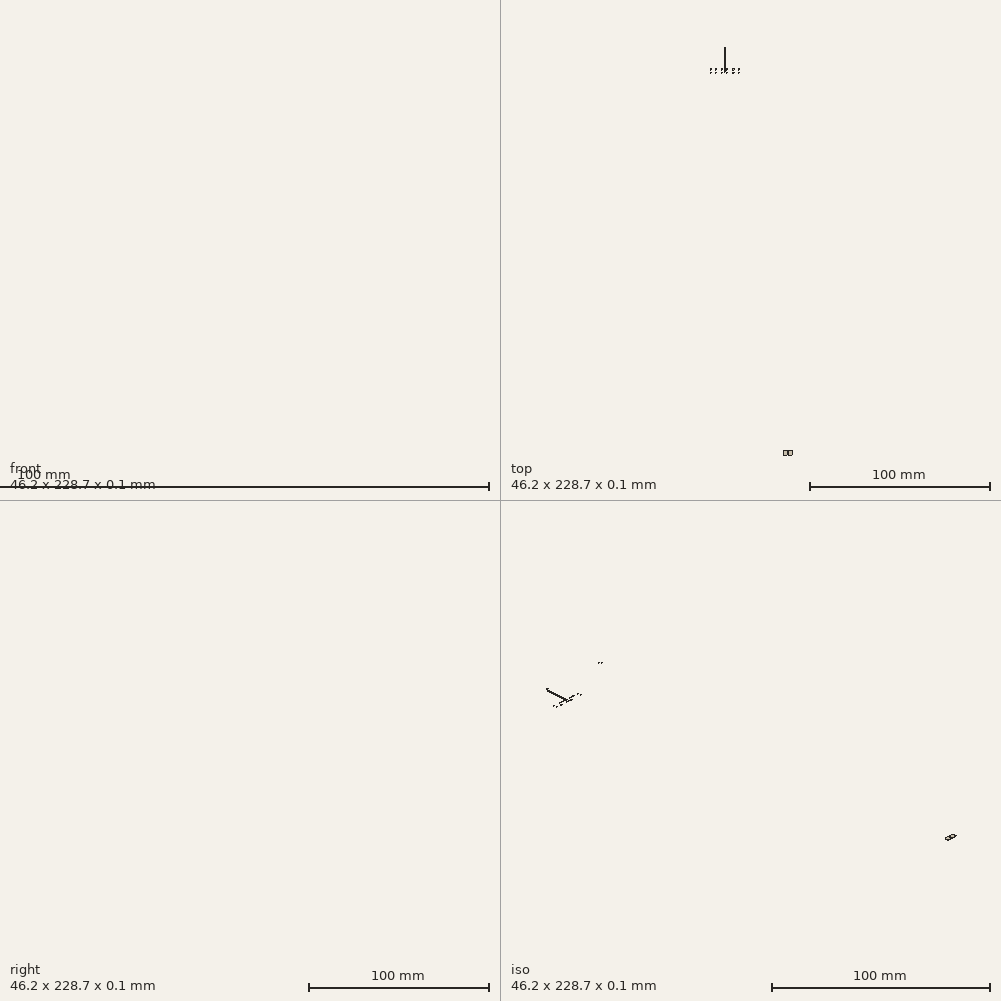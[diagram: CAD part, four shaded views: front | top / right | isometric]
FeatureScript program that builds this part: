
annotation { "Feature Type Name" : "Feature", "Feature Type Description" : "" }
export const myFeature = defineFeature(function(context is Context, id is Id, definition is map)
    precondition{}
    {
        {
            var Q0;
            Q0=qCreatedBy(makeId("Top.planeOp"),FACE);
            var sketch = newSketch(context, id + "F0", { "sketchPlane" : qUnion([Q0])});
            skLineSegment(sketch, "E0.bottom", {"start": v(0, 0) * mm, "end": v(3.5, 0) * mm, "construction": true});
            skLineSegment(sketch, "E0.top", {"start": v(0, 2.4) * mm, "end": v(3.5, 2.4) * mm, "construction": true});
            skLineSegment(sketch, "E0.left", {"start": v(0, 0) * mm, "end": v(0, 2.4) * mm, "construction": true});
            skLineSegment(sketch, "E0.right", {"start": v(3.5, 0) * mm, "end": v(3.5, 0.27) * mm, "construction": true});
            skLineSegment(sketch, "E1.bottom", {"start": v(0, 2.4) * mm, "end": v(0.6, 2.4) * mm});
            skLineSegment(sketch, "E1.top", {"start": v(0, 1.8) * mm, "end": v(0.6, 1.8) * mm});
            skLineSegment(sketch, "E1.left", {"start": v(0, 2.4) * mm, "end": v(0, 1.8) * mm});
            skLineSegment(sketch, "E1.right", {"start": v(0.6, 2.4) * mm, "end": v(0.6, 1.8) * mm});
            skLineSegment(sketch, "E2.bottom", {"start": v(0, 0) * mm, "end": v(0.6, 0) * mm});
            skLineSegment(sketch, "E2.top", {"start": v(0, 0.6) * mm, "end": v(0.6, 0.6) * mm});
            skLineSegment(sketch, "E2.left", {"start": v(0, 0) * mm, "end": v(0, 0.6) * mm});
            skLineSegment(sketch, "E2.right", {"start": v(0.6, 0) * mm, "end": v(0.6, 0.6) * mm});
            skLineSegment(sketch, "E3.bottom", {"start": v(3.5, 2.4) * mm, "end": v(2.9, 2.4) * mm});
            skLineSegment(sketch, "E3.top", {"start": v(3.5, 1.8) * mm, "end": v(2.9, 1.8) * mm});
            skLineSegment(sketch, "E3.left", {"start": v(3.5, 2.4) * mm, "end": v(3.5, 2.13) * mm});
            skLineSegment(sketch, "E3.right", {"start": v(2.9, 2.4) * mm, "end": v(2.9, 1.8) * mm});
            skLineSegment(sketch, "E4.bottom", {"start": v(3.5, 0) * mm, "end": v(2.9, 0) * mm});
            skLineSegment(sketch, "E4.top", {"start": v(3.5, 0.6) * mm, "end": v(2.9, 0.6) * mm});
            skLineSegment(sketch, "E4.left", {"start": v(3.5, 0) * mm, "end": v(3.5, 0.27) * mm});
            skLineSegment(sketch, "E4.right", {"start": v(2.9, 0) * mm, "end": v(2.9, 0.6) * mm});
            skLineSegment(sketch, "E5", {"start": v(0, 0) * mm, "end": v(16.26, 0) * mm, "construction": true});
            skLineSegment(sketch, "E6.bottom", {"start": v(12.76, 0) * mm, "end": v(16.26, 0) * mm, "construction": true});
            skLineSegment(sketch, "E6.top", {"start": v(12.76, 2.4) * mm, "end": v(16.26, 2.4) * mm, "construction": true});
            skLineSegment(sketch, "E6.right", {"start": v(16.26, 0) * mm, "end": v(16.26, 2.4) * mm, "construction": true});
            skLineSegment(sketch, "E7.bottom", {"start": v(12.76, 2.4) * mm, "end": v(13.36, 2.4) * mm});
            skLineSegment(sketch, "E7.top", {"start": v(12.76, 1.8) * mm, "end": v(13.36, 1.8) * mm});
            skLineSegment(sketch, "E7.left", {"start": v(12.76, 2.4) * mm, "end": v(12.76, 2.13) * mm});
            skLineSegment(sketch, "E7.right", {"start": v(13.36, 2.4) * mm, "end": v(13.36, 1.8) * mm});
            skLineSegment(sketch, "E8.bottom", {"start": v(12.76, 0) * mm, "end": v(13.36, 0) * mm});
            skLineSegment(sketch, "E8.top", {"start": v(12.76, 0.6) * mm, "end": v(13.36, 0.6) * mm});
            skLineSegment(sketch, "E8.left", {"start": v(12.76, 0) * mm, "end": v(12.76, 0.27) * mm});
            skLineSegment(sketch, "E8.right", {"start": v(13.36, 0) * mm, "end": v(13.36, 0.6) * mm});
            skLineSegment(sketch, "E9.bottom", {"start": v(16.26, 2.4) * mm, "end": v(15.66, 2.4) * mm});
            skLineSegment(sketch, "E9.top", {"start": v(16.26, 1.8) * mm, "end": v(15.66, 1.8) * mm});
            skLineSegment(sketch, "E9.left", {"start": v(16.26, 2.4) * mm, "end": v(16.26, 1.8) * mm});
            skLineSegment(sketch, "E9.right", {"start": v(15.66, 2.4) * mm, "end": v(15.66, 1.8) * mm});
            skLineSegment(sketch, "E10.bottom", {"start": v(16.26, 0) * mm, "end": v(15.66, 0) * mm});
            skLineSegment(sketch, "E10.top", {"start": v(16.26, 0.6) * mm, "end": v(15.66, 0.6) * mm});
            skLineSegment(sketch, "E10.left", {"start": v(16.26, 0) * mm, "end": v(16.26, 0.6) * mm});
            skLineSegment(sketch, "E10.right", {"start": v(15.66, 0) * mm, "end": v(15.66, 0.6) * mm});
            skLineSegment(sketch, "E11.bottom", {"start": v(6.38, 0) * mm, "end": v(9.88, 0) * mm, "construction": true});
            skLineSegment(sketch, "E11.top", {"start": v(6.38, 2.4) * mm, "end": v(9.88, 2.4) * mm, "construction": true});
            skLineSegment(sketch, "E11.left", {"start": v(6.38, 0) * mm, "end": v(6.38, 0.27) * mm, "construction": true});
            skLineSegment(sketch, "E12.bottom", {"start": v(6.38, 2.4) * mm, "end": v(6.98, 2.4) * mm});
            skLineSegment(sketch, "E12.top", {"start": v(6.38, 1.8) * mm, "end": v(6.98, 1.8) * mm});
            skLineSegment(sketch, "E12.left", {"start": v(6.38, 2.4) * mm, "end": v(6.38, 2.13) * mm});
            skLineSegment(sketch, "E12.right", {"start": v(6.98, 2.4) * mm, "end": v(6.98, 1.8) * mm});
            skLineSegment(sketch, "E13.bottom", {"start": v(6.38, 0) * mm, "end": v(6.98, 0) * mm});
            skLineSegment(sketch, "E13.top", {"start": v(6.38, 0.6) * mm, "end": v(6.98, 0.6) * mm});
            skLineSegment(sketch, "E13.left", {"start": v(6.38, 0) * mm, "end": v(6.38, 0.27) * mm});
            skLineSegment(sketch, "E13.right", {"start": v(6.98, 0) * mm, "end": v(6.98, 0.6) * mm});
            skLineSegment(sketch, "E14.bottom", {"start": v(9.88, 2.4) * mm, "end": v(9.28, 2.4) * mm});
            skLineSegment(sketch, "E14.top", {"start": v(9.88, 1.8) * mm, "end": v(9.28, 1.8) * mm});
            skLineSegment(sketch, "E14.left", {"start": v(9.88, 2.4) * mm, "end": v(9.88, 2.13) * mm});
            skLineSegment(sketch, "E14.right", {"start": v(9.28, 2.4) * mm, "end": v(9.28, 1.8) * mm});
            skLineSegment(sketch, "E15.bottom", {"start": v(9.88, 0) * mm, "end": v(9.28, 0) * mm});
            skLineSegment(sketch, "E15.top", {"start": v(9.88, 0.6) * mm, "end": v(9.28, 0.6) * mm});
            skLineSegment(sketch, "E15.left", {"start": v(9.88, 0) * mm, "end": v(9.88, 0.27) * mm});
            skLineSegment(sketch, "E15.right", {"start": v(9.28, 0) * mm, "end": v(9.28, 0.6) * mm});
            skPoint(sketch, "E16", {"position": v(8.13, 0) * mm});
            skLineSegment(sketch, "E17.bottom", {"start": v(3.5, 2.13) * mm, "end": v(6.38, 2.13) * mm});
            skLineSegment(sketch, "E17.top", {"start": v(3.5, 2.06) * mm, "end": v(6.38, 2.06) * mm});
            skLineSegment(sketch, "E18.bottom", {"start": v(3.5, 0.33) * mm, "end": v(6.38, 0.33) * mm});
            skLineSegment(sketch, "E18.top", {"start": v(3.5, 0.27) * mm, "end": v(6.38, 0.27) * mm});
            skLineSegment(sketch, "E19.trimOffspring", {"start": v(3.5, 2.13) * mm, "end": v(3.5, 2.4) * mm, "construction": true});
            skLineSegment(sketch, "E20.trimOffspring", {"start": v(3.5, 2.06) * mm, "end": v(3.5, 1.8) * mm});
            skLineSegment(sketch, "E21.trimOffspring", {"start": v(6.38, 2.13) * mm, "end": v(6.38, 2.4) * mm, "construction": true});
            skLineSegment(sketch, "E22.trimOffspring", {"start": v(6.38, 2.06) * mm, "end": v(6.38, 1.8) * mm});
            skLineSegment(sketch, "E23.trimOffspring", {"start": v(3.5, 0.33) * mm, "end": v(3.5, 2.06) * mm, "construction": true});
            skLineSegment(sketch, "E24.trimOffspring", {"start": v(3.5, 0.33) * mm, "end": v(3.5, 0.6) * mm});
            skLineSegment(sketch, "E25.trimOffspring", {"start": v(6.38, 0.33) * mm, "end": v(6.38, 2.06) * mm, "construction": true});
            skLineSegment(sketch, "E26.trimOffspring", {"start": v(6.38, 0.33) * mm, "end": v(6.38, 0.6) * mm});
            skLineSegment(sketch, "E27.bottom", {"start": v(9.88, 2.13) * mm, "end": v(12.76, 2.13) * mm});
            skLineSegment(sketch, "E27.top", {"start": v(9.88, 2.07) * mm, "end": v(12.76, 2.07) * mm});
            skLineSegment(sketch, "E28.bottom", {"start": v(9.88, 0.33) * mm, "end": v(12.76, 0.33) * mm});
            skLineSegment(sketch, "E28.top", {"start": v(9.88, 0.27) * mm, "end": v(12.76, 0.27) * mm});
            skLineSegment(sketch, "E29.trimOffspring", {"start": v(9.88, 0.33) * mm, "end": v(9.88, 0.6) * mm, "construction": true});
            skLineSegment(sketch, "E30.trimOffspring", {"start": v(9.88, 0.33) * mm, "end": v(9.88, 0.6) * mm});
            skLineSegment(sketch, "E31.trimOffspring", {"start": v(12.76, 0.33) * mm, "end": v(12.76, 2.07) * mm, "construction": true});
            skLineSegment(sketch, "E32.trimOffspring", {"start": v(12.76, 0.33) * mm, "end": v(12.76, 0.6) * mm});
            skLineSegment(sketch, "E33.trimOffspring", {"start": v(12.76, 2.13) * mm, "end": v(12.76, 2.4) * mm, "construction": true});
            skLineSegment(sketch, "E34.trimOffspring", {"start": v(12.76, 2.07) * mm, "end": v(12.76, 1.8) * mm});
            skLineSegment(sketch, "E35.trimOffspring", {"start": v(9.88, 2.13) * mm, "end": v(9.88, 2.4) * mm, "construction": true});
            skLineSegment(sketch, "E36.trimOffspring", {"start": v(9.88, 2.07) * mm, "end": v(9.88, 1.8) * mm});
            skLineSegment(sketch, "E37.bottom", {"start": v(6.98, 2.13) * mm, "end": v(7.92, 2.13) * mm});
            skLineSegment(sketch, "E37.top", {"start": v(6.98, 2.07) * mm, "end": v(7.92, 2.07) * mm});
            skLineSegment(sketch, "E37.left", {"start": v(6.98, 2.13) * mm, "end": v(6.98, 2.07) * mm});
            skLineSegment(sketch, "E37.right", {"start": v(7.92, 2.13) * mm, "end": v(7.92, 2.07) * mm});
            skLineSegment(sketch, "E38.bottom", {"start": v(9.28, 0.33) * mm, "end": v(8.33, 0.33) * mm});
            skLineSegment(sketch, "E38.top", {"start": v(9.28, 0.27) * mm, "end": v(8.33, 0.27) * mm});
            skLineSegment(sketch, "E38.left", {"start": v(9.28, 0.33) * mm, "end": v(9.28, 0.27) * mm});
            skLineSegment(sketch, "E38.right", {"start": v(8.33, 0.33) * mm, "end": v(8.33, 0.27) * mm});
            skLineSegment(sketch, "E39.bottom", {"start": v(7.92, 2.07) * mm, "end": v(8, 2.07) * mm});
            skLineSegment(sketch, "E39.top", {"start": v(7.92, 2.4) * mm, "end": v(8, 2.4) * mm});
            skLineSegment(sketch, "E39.left", {"start": v(7.92, 2.07) * mm, "end": v(7.92, 2.4) * mm});
            skLineSegment(sketch, "E39.right", {"start": v(8, 2.07) * mm, "end": v(8, 2.4) * mm});
            skLineSegment(sketch, "E40.bottom", {"start": v(8.33, 0.27) * mm, "end": v(8.26, 0.27) * mm});
            skLineSegment(sketch, "E40.top", {"start": v(8.33, 2.4) * mm, "end": v(8.26, 2.4) * mm});
            skLineSegment(sketch, "E40.left", {"start": v(8.33, 0.27) * mm, "end": v(8.33, 2.4) * mm});
            skLineSegment(sketch, "E40.right", {"start": v(8.26, 0.27) * mm, "end": v(8.26, 2.4) * mm});
            skLineSegment(sketch, "E41.left", {"start": v(7.92, 2.4) * mm, "end": v(7.92, 2.4) * mm});
            skLineSegment(sketch, "E41.right", {"start": v(8, 2.4) * mm, "end": v(8, 2.4) * mm});
            skLineSegment(sketch, "E42.top", {"start": v(7.92, 5.46) * mm, "end": v(8, 5.46) * mm});
            skLineSegment(sketch, "E42.left", {"start": v(7.92, 2.4) * mm, "end": v(7.92, 5.46) * mm});
            skLineSegment(sketch, "E42.right", {"start": v(8, 2.4) * mm, "end": v(8, 5.46) * mm});
            skLineSegment(sketch, "E43.bottom", {"start": v(8.26, 2.4) * mm, "end": v(8.33, 2.4) * mm});
            skLineSegment(sketch, "E43.top", {"start": v(8.26, 5.46) * mm, "end": v(8.33, 5.46) * mm});
            skLineSegment(sketch, "E43.left", {"start": v(8.26, 2.4) * mm, "end": v(8.26, 5.46) * mm});
            skLineSegment(sketch, "E43.right", {"start": v(8.33, 2.4) * mm, "end": v(8.33, 5.46) * mm});
            skLineSegment(sketch, "E44.top", {"start": v(8, 15.48) * mm, "end": v(9.2, 15.48) * mm});
            skLineSegment(sketch, "E44.left", {"start": v(7.92, 5.46) * mm, "end": v(7.92, 14.21) * mm});
            skLineSegment(sketch, "E44.right", {"start": v(8, 5.46) * mm, "end": v(8, 14.13) * mm});
            skLineSegment(sketch, "E45.top", {"start": v(8.33, 15.15) * mm, "end": v(8.34, 15.15) * mm});
            skLineSegment(sketch, "E45.left", {"start": v(8.26, 5.46) * mm, "end": v(8.26, 13.88) * mm});
            skLineSegment(sketch, "E45.right", {"start": v(8.33, 5.46) * mm, "end": v(8.33, 13.8) * mm});
            skLineSegment(sketch, "E46.bottom", {"start": v(9.2, 15.48) * mm, "end": v(42.47, 15.48) * mm});
            skLineSegment(sketch, "E46.top", {"start": v(9.27, 15.4) * mm, "end": v(42.4, 15.4) * mm});
            skLineSegment(sketch, "E46.left", {"start": v(7.92, 15.4) * mm, "end": v(7.92, 14.21) * mm});
            skLineSegment(sketch, "E47.bottom", {"start": v(9.53, 15.15) * mm, "end": v(42.14, 15.15) * mm});
            skLineSegment(sketch, "E47.top", {"start": v(9.6, 15.07) * mm, "end": v(42.06, 15.07) * mm});
            skLineSegment(sketch, "E47.left", {"start": v(8.26, 15.07) * mm, "end": v(8.26, 15.07) * mm});
            skPoint(sketch, "E48.visualSharp", {"position": v(7.92, 15.48) * mm});
            skArc(sketch, "E48.filletArc", {"start": v(9.2, 15.48) * mm, "mid": v(8.3, 15.1) * mm, "end": v(7.92, 14.21) * mm});
            skPoint(sketch, "E49.visualSharp", {"position": v(8, 15.4) * mm});
            skArc(sketch, "E49.filletArc", {"start": v(9.27, 15.4) * mm, "mid": v(8.37, 15.03) * mm, "end": v(8, 14.13) * mm});
            skPoint(sketch, "E50.visualSharp", {"position": v(8.26, 15.15) * mm});
            skArc(sketch, "E50.filletArc", {"start": v(9.53, 15.15) * mm, "mid": v(8.63, 14.78) * mm, "end": v(8.26, 13.88) * mm});
            skPoint(sketch, "E51.visualSharp", {"position": v(8.33, 15.07) * mm});
            skArc(sketch, "E51.filletArc", {"start": v(9.6, 15.07) * mm, "mid": v(8.7, 14.7) * mm, "end": v(8.33, 13.8) * mm});
            skLineSegment(sketch, "E52.top", {"start": v(43.74, -210.63) * mm, "end": v(43.66, -210.63) * mm});
            skLineSegment(sketch, "E52.left", {"start": v(43.74, 14.21) * mm, "end": v(43.74, -210.63) * mm});
            skLineSegment(sketch, "E52.right", {"start": v(43.66, 14.13) * mm, "end": v(43.66, -210.63) * mm});
            skLineSegment(sketch, "E53.bottom", {"start": v(43.33, 15.15) * mm, "end": v(43.32, 15.15) * mm});
            skLineSegment(sketch, "E53.top", {"start": v(43.4, -210.63) * mm, "end": v(43.33, -210.63) * mm});
            skLineSegment(sketch, "E53.left", {"start": v(43.4, 13.88) * mm, "end": v(43.4, -210.63) * mm});
            skLineSegment(sketch, "E53.right", {"start": v(43.33, 13.8) * mm, "end": v(43.33, -210.63) * mm});
            skPoint(sketch, "E54.visualSharp", {"position": v(43.33, 15.07) * mm});
            skArc(sketch, "E54.filletArc", {"start": v(43.33, 13.8) * mm, "mid": v(42.96, 14.7) * mm, "end": v(42.06, 15.07) * mm});
            skPoint(sketch, "E55.visualSharp", {"position": v(43.4, 15.15) * mm});
            skArc(sketch, "E55.filletArc", {"start": v(43.4, 13.88) * mm, "mid": v(43.04, 14.78) * mm, "end": v(42.14, 15.15) * mm});
            skPoint(sketch, "E56.visualSharp", {"position": v(43.74, 15.48) * mm});
            skArc(sketch, "E56.filletArc", {"start": v(43.74, 14.21) * mm, "mid": v(43.37, 15.1) * mm, "end": v(42.47, 15.48) * mm});
            skPoint(sketch, "E57.visualSharp", {"position": v(43.66, 15.4) * mm});
            skArc(sketch, "E57.filletArc", {"start": v(43.66, 14.13) * mm, "mid": v(43.3, 15.03) * mm, "end": v(42.4, 15.4) * mm});
            skLineSegment(sketch, "E58.top", {"start": v(43.4, -213.17) * mm, "end": v(40.87, -213.17) * mm});
            skLineSegment(sketch, "E58.left", {"start": v(43.4, -210.63) * mm, "end": v(43.4, -213.17) * mm});
            skLineSegment(sketch, "E58.right", {"start": v(40.87, -210.63) * mm, "end": v(40.87, -213.17) * mm});
            skLineSegment(sketch, "E59.bottom", {"start": v(43.66, -210.63) * mm, "end": v(46.2, -210.63) * mm});
            skLineSegment(sketch, "E59.top", {"start": v(43.66, -213.17) * mm, "end": v(46.2, -213.17) * mm});
            skLineSegment(sketch, "E59.left", {"start": v(43.66, -210.63) * mm, "end": v(43.66, -213.17) * mm});
            skLineSegment(sketch, "E59.right", {"start": v(46.2, -210.63) * mm, "end": v(46.2, -213.17) * mm});
            skLineSegment(sketch, "E60.bottom", {"start": v(40.87, -210.63) * mm, "end": v(43.4, -210.63) * mm});
            skSolve(sketch);
        }
        {
            var Q0;
            Q0 = qSketchRegion(id + "F0", true);
            extrude(context, id + "F1", {"entities" : qUnion([Q0]), "depth" : 0.05 * mm});
        }
    });
